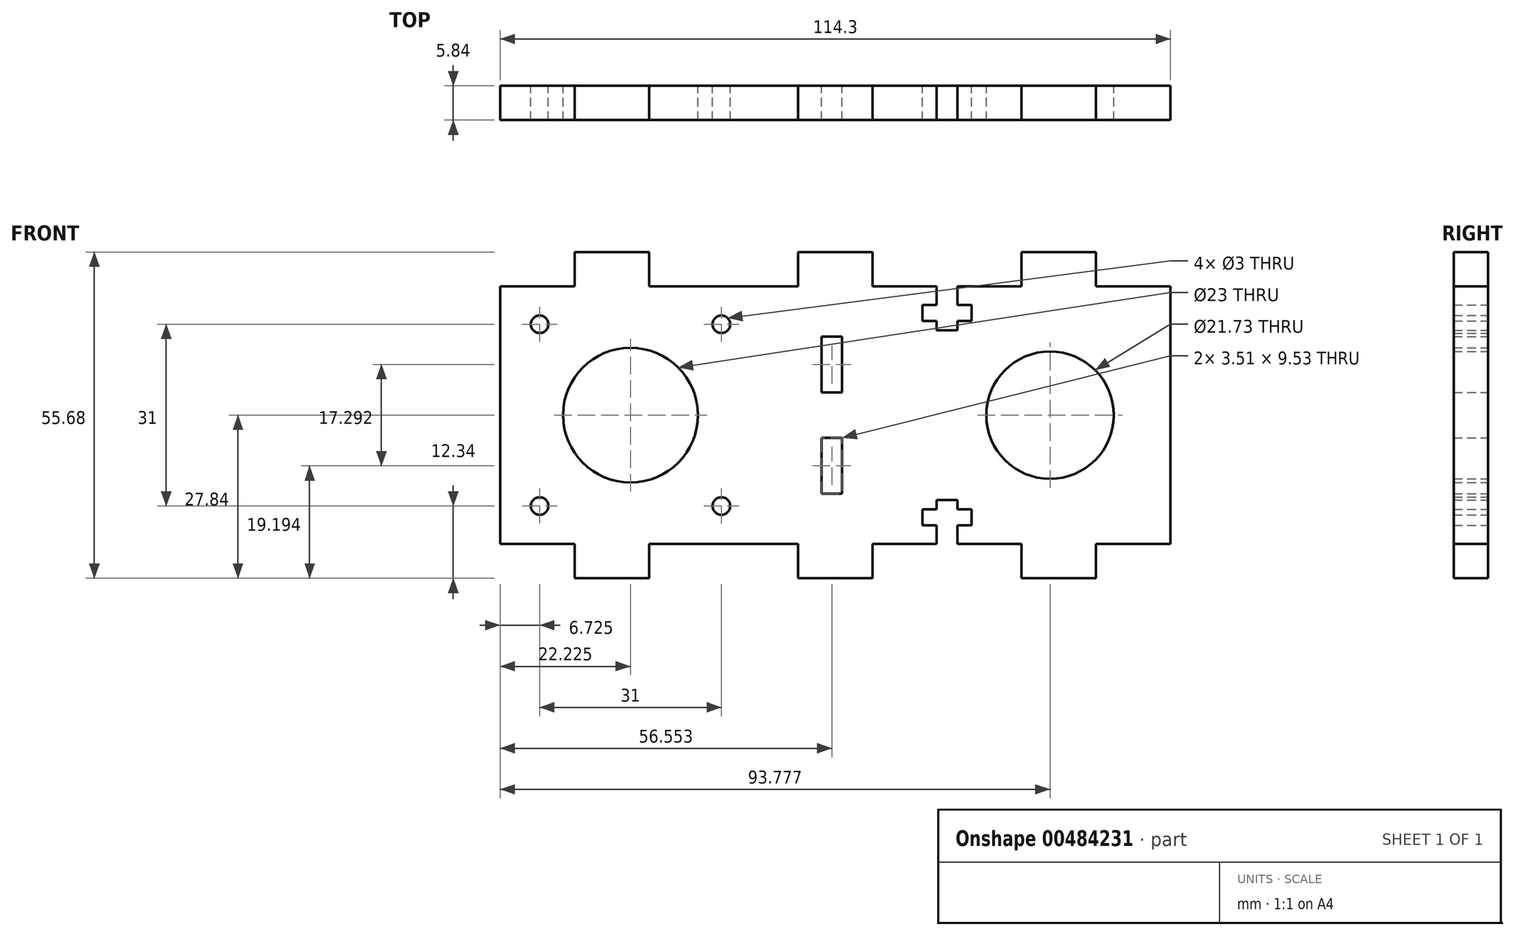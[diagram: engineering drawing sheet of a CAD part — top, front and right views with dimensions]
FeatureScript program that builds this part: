
annotation { "Feature Type Name" : "Feature", "Feature Type Description" : "" }
export const myFeature = defineFeature(function(context is Context, id is Id, definition is map)
    precondition{}
    {
        {
            var Q0;
            Q0=qCreatedBy(makeId("Front.planeOp"),FACE);
            var sketch = newSketch(context, id + "F0", { "sketchPlane" : qUnion([Q0])});
            skLineSegment(sketch, "E0.bottom", {"start": v(-57.15, 22) * mm, "end": v(-44.45, 22) * mm});
            skLineSegment(sketch, "E0.left", {"start": v(-57.15, 22) * mm, "end": v(-57.15, -22) * mm});
            skLineSegment(sketch, "E0.right", {"start": v(57.15, 22) * mm, "end": v(57.15, -22) * mm});
            skPoint(sketch, "E0.middle", {"position": v(0, 0) * mm});
            skCircle(sketch, "E1", {"center": v(-34.93, 0) * mm, "radius": 11.5 * mm});
            skCircle(sketch, "E2", {"center": v(36.63, 0) * mm, "radius": 10.86 * mm});
            skCircle(sketch, "E3", {"center": v(-50.43, 15.5) * mm, "radius": 1.5 * mm});
            skLineSegment(sketch, "E4", {"start": v(-34.93, 0) * mm, "end": v(-34.93, 11.5) * mm, "construction": true});
            skLineSegment(sketch, "E5", {"start": v(-34.93, 0) * mm, "end": v(-46.43, 0) * mm, "construction": true});
            skCircle(sketch, "E6.MirrorC", {"center": v(-19.43, 15.5) * mm, "radius": 1.5 * mm});
            skCircle(sketch, "E7.MirrorC", {"center": v(-19.43, -15.5) * mm, "radius": 1.5 * mm});
            skCircle(sketch, "E8.MirrorC", {"center": v(-50.43, -15.5) * mm, "radius": 1.5 * mm});
            skCircle(sketch, "E9", {"center": v(-34.93, 0) * mm, "radius": 5 * mm, "construction": true});
            skCircle(sketch, "E10", {"center": v(36.63, 0) * mm, "radius": 12.5 * mm, "construction": true});
            skLineSegment(sketch, "E11", {"start": v(-35.45, 4.97) * mm, "end": v(35.32, 12.43) * mm, "construction": true});
            skLineSegment(sketch, "E12.MirrorCS", {"start": v(-35.45, -4.97) * mm, "end": v(35.32, -12.43) * mm, "construction": true});
            skLineSegment(sketch, "E13", {"start": v(-0.6, 0) * mm, "end": v(-0.6, 12.84) * mm, "construction": true});
            skLineSegment(sketch, "E14.bottom", {"start": v(1.16, 13.4) * mm, "end": v(-2.35, 13.4) * mm});
            skLineSegment(sketch, "E14.top", {"start": v(1.16, 3.88) * mm, "end": v(-2.35, 3.88) * mm});
            skLineSegment(sketch, "E14.left", {"start": v(1.16, 13.4) * mm, "end": v(1.16, 3.88) * mm});
            skLineSegment(sketch, "E14.right", {"start": v(-2.35, 13.4) * mm, "end": v(-2.35, 3.88) * mm});
            skPoint(sketch, "E14.middle", {"position": v(-0.6, 8.65) * mm});
            skLineSegment(sketch, "E15.MirrorCS", {"start": v(1.16, -13.4) * mm, "end": v(-2.35, -13.4) * mm});
            skPoint(sketch, "E16.MirrorP", {"position": v(-0.6, -8.65) * mm});
            skLineSegment(sketch, "E17.MirrorCS", {"start": v(1.16, -13.4) * mm, "end": v(1.16, -3.88) * mm});
            skLineSegment(sketch, "E18.MirrorCS", {"start": v(1.16, -3.88) * mm, "end": v(-2.35, -3.88) * mm});
            skLineSegment(sketch, "E19.MirrorCS", {"start": v(-2.35, -13.4) * mm, "end": v(-2.35, -3.88) * mm});
            skLineSegment(sketch, "E20.top", {"start": v(-44.45, 27.84) * mm, "end": v(-31.75, 27.84) * mm});
            skLineSegment(sketch, "E20.left", {"start": v(-44.45, 22) * mm, "end": v(-44.45, 27.84) * mm});
            skLineSegment(sketch, "E20.right", {"start": v(-31.75, 22) * mm, "end": v(-31.75, 27.84) * mm});
            skPoint(sketch, "E20.middle", {"position": v(-38.1, 24.92) * mm});
            skLineSegment(sketch, "E21.trimOffspring", {"start": v(-31.75, 22) * mm, "end": v(-20.8, 22) * mm});
            skLineSegment(sketch, "E22.MirrorCS", {"start": v(44.45, 27.84) * mm, "end": v(31.75, 27.84) * mm});
            skLineSegment(sketch, "E23.MirrorCS", {"start": v(31.75, 22) * mm, "end": v(31.75, 27.84) * mm});
            skLineSegment(sketch, "E24.MirrorCS", {"start": v(44.45, 22) * mm, "end": v(44.45, 27.84) * mm});
            skPoint(sketch, "E25.MirrorP", {"position": v(38.1, 24.92) * mm});
            skLineSegment(sketch, "E26.MirrorCS", {"start": v(44.45, -22) * mm, "end": v(44.45, -27.84) * mm});
            skLineSegment(sketch, "E27.MirrorCS", {"start": v(-44.45, -27.84) * mm, "end": v(-31.75, -27.84) * mm});
            skLineSegment(sketch, "E28.MirrorCS", {"start": v(31.75, -22) * mm, "end": v(31.75, -27.84) * mm});
            skPoint(sketch, "E29.MirrorP", {"position": v(38.1, -24.92) * mm});
            skLineSegment(sketch, "E30.MirrorCS", {"start": v(44.45, -27.84) * mm, "end": v(31.75, -27.84) * mm});
            skPoint(sketch, "E31.MirrorP", {"position": v(-38.1, -24.92) * mm});
            skLineSegment(sketch, "E32.MirrorCS", {"start": v(-31.75, -22) * mm, "end": v(-31.75, -27.84) * mm});
            skLineSegment(sketch, "E33.MirrorCS", {"start": v(-44.45, -22) * mm, "end": v(-44.45, -27.84) * mm});
            skLineSegment(sketch, "E34.trimOffspring", {"start": v(-31.75, -22) * mm, "end": v(-20.8, -22) * mm});
            skLineSegment(sketch, "E35.trimOffspring", {"start": v(44.45, -22) * mm, "end": v(57.15, -22) * mm});
            skLineSegment(sketch, "E36.trimOffspring", {"start": v(44.45, 22) * mm, "end": v(57.15, 22) * mm});
            skLineSegment(sketch, "E37", {"start": v(-57.15, -22) * mm, "end": v(-44.45, -22) * mm});
            skLineSegment(sketch, "E38.top", {"start": v(-6.35, 27.84) * mm, "end": v(6.35, 27.84) * mm});
            skLineSegment(sketch, "E38.left", {"start": v(-6.35, 22) * mm, "end": v(-6.35, 27.84) * mm});
            skLineSegment(sketch, "E38.right", {"start": v(6.35, 22) * mm, "end": v(6.35, 27.84) * mm});
            skPoint(sketch, "E38.middle", {"position": v(0, 24.92) * mm});
            skLineSegment(sketch, "E39.trimOffspring", {"start": v(6.35, 22) * mm, "end": v(17.3, 22) * mm});
            skLineSegment(sketch, "E40.MirrorCS", {"start": v(6.35, -22) * mm, "end": v(6.35, -27.84) * mm});
            skPoint(sketch, "E41.MirrorP", {"position": v(0, -24.92) * mm});
            skLineSegment(sketch, "E42.MirrorCS", {"start": v(-6.35, -22) * mm, "end": v(-6.35, -27.84) * mm});
            skLineSegment(sketch, "E43.MirrorCS", {"start": v(-6.35, -27.84) * mm, "end": v(6.35, -27.84) * mm});
            skLineSegment(sketch, "E44.trimOffspring", {"start": v(6.35, -22) * mm, "end": v(17.3, -22) * mm});
            skLineSegment(sketch, "E45", {"start": v(-19.05, 22) * mm, "end": v(-19.05, -22) * mm, "construction": true});
            skPoint(sketch, "E46.middle", {"position": v(-19.05, -20.41) * mm});
            skPoint(sketch, "E47.middle", {"position": v(-19.05, -17.44) * mm});
            skPoint(sketch, "E48.middle", {"position": v(-19.05, -15.25) * mm});
            skLineSegment(sketch, "E49", {"start": v(-20.82, -16.05) * mm, "end": v(-20.8, -16.05) * mm});
            skLineSegment(sketch, "E50.trimOffspring", {"start": v(-17.3, -22) * mm, "end": v(-6.35, -22) * mm});
            skPoint(sketch, "E51.MirrorP", {"position": v(19.05, -15.25) * mm});
            skLineSegment(sketch, "E52.MirrorCS", {"start": v(17.3, -16.05) * mm, "end": v(17.3, -14.46) * mm});
            skLineSegment(sketch, "E53.MirrorCS", {"start": v(23.22, -18.83) * mm, "end": v(20.8, -18.83) * mm});
            skLineSegment(sketch, "E54.MirrorCS", {"start": v(17.3, -16.05) * mm, "end": v(14.88, -16.05) * mm});
            skLineSegment(sketch, "E55.MirrorCS", {"start": v(14.88, -18.83) * mm, "end": v(14.88, -16.05) * mm});
            skPoint(sketch, "E56.MirrorP", {"position": v(19.05, -17.44) * mm});
            skPoint(sketch, "E57.MirrorP", {"position": v(19.05, -20.41) * mm});
            skLineSegment(sketch, "E58.MirrorCS", {"start": v(20.8, -16.05) * mm, "end": v(20.8, -14.46) * mm});
            skLineSegment(sketch, "E59.MirrorCS", {"start": v(23.22, -18.83) * mm, "end": v(23.22, -16.05) * mm});
            skLineSegment(sketch, "E60.MirrorCS", {"start": v(23.22, -16.05) * mm, "end": v(20.8, -16.05) * mm});
            skLineSegment(sketch, "E61.MirrorCS", {"start": v(20.8, -14.46) * mm, "end": v(17.3, -14.46) * mm});
            skLineSegment(sketch, "E62.MirrorCS", {"start": v(20.8, -22) * mm, "end": v(20.8, -18.83) * mm});
            skLineSegment(sketch, "E63.MirrorCS", {"start": v(17.3, -18.83) * mm, "end": v(14.88, -18.83) * mm});
            skLineSegment(sketch, "E64.MirrorCS", {"start": v(17.3, -22) * mm, "end": v(17.3, -18.83) * mm});
            skLineSegment(sketch, "E65.trimOffspring", {"start": v(20.8, -22) * mm, "end": v(31.75, -22) * mm});
            skLineSegment(sketch, "E66.MirrorCS", {"start": v(23.22, 16.05) * mm, "end": v(20.8, 16.05) * mm});
            skLineSegment(sketch, "E67.MirrorCS", {"start": v(17.3, 18.83) * mm, "end": v(14.88, 18.83) * mm});
            skLineSegment(sketch, "E68.MirrorCS", {"start": v(23.22, 18.83) * mm, "end": v(20.8, 18.83) * mm});
            skLineSegment(sketch, "E69.MirrorCS", {"start": v(17.3, 16.05) * mm, "end": v(17.3, 14.46) * mm});
            skLineSegment(sketch, "E70.MirrorCS", {"start": v(17.3, 16.05) * mm, "end": v(14.88, 16.05) * mm});
            skLineSegment(sketch, "E71.MirrorCS", {"start": v(20.8, 16.05) * mm, "end": v(20.8, 14.46) * mm});
            skLineSegment(sketch, "E72.MirrorCS", {"start": v(-20.82, 16.05) * mm, "end": v(-20.8, 16.05) * mm});
            skLineSegment(sketch, "E73.MirrorCS", {"start": v(20.8, 14.46) * mm, "end": v(17.3, 14.46) * mm});
            skPoint(sketch, "E74.MirrorP", {"position": v(19.05, 20.41) * mm});
            skLineSegment(sketch, "E75.MirrorCS", {"start": v(14.88, 18.83) * mm, "end": v(14.88, 16.05) * mm});
            skPoint(sketch, "E76.MirrorP", {"position": v(-19.05, 20.41) * mm});
            skLineSegment(sketch, "E77.MirrorCS", {"start": v(23.22, 18.83) * mm, "end": v(23.22, 16.05) * mm});
            skLineSegment(sketch, "E78.MirrorCS", {"start": v(-17.3, 22) * mm, "end": v(-6.35, 22) * mm});
            skLineSegment(sketch, "E79.MirrorCS", {"start": v(20.8, 22) * mm, "end": v(20.8, 18.83) * mm});
            skPoint(sketch, "E80.MirrorP", {"position": v(19.05, 15.25) * mm});
            skLineSegment(sketch, "E81.MirrorCS", {"start": v(17.3, 22) * mm, "end": v(17.3, 18.83) * mm});
            skPoint(sketch, "E82.MirrorP", {"position": v(-19.05, 15.25) * mm});
            skPoint(sketch, "E83.MirrorP", {"position": v(-19.05, 17.44) * mm});
            skPoint(sketch, "E84.MirrorP", {"position": v(19.05, 17.44) * mm});
            skLineSegment(sketch, "E85.trimOffspring", {"start": v(20.8, 22) * mm, "end": v(31.75, 22) * mm});
            skLineSegment(sketch, "E86", {"start": v(-20.8, -22) * mm, "end": v(-17.3, -22) * mm});
            skLineSegment(sketch, "E87", {"start": v(-20.8, 22) * mm, "end": v(-17.3, 22) * mm});
            skPoint(sketch, "E88.orphan", {"position": v(-20.8, 14.46) * mm});
            skPoint(sketch, "E89.MirrorCS.end.orphan", {"position": v(-23.22, 16.05) * mm});
            skPoint(sketch, "E90.MirrorCS.end.orphan", {"position": v(-20.8, 18.83) * mm});
            skPoint(sketch, "E90.MirrorCS.start.orphan", {"position": v(-23.22, 18.83) * mm});
            skPoint(sketch, "E91.MirrorCS.start.orphan", {"position": v(-17.3, 18.83) * mm});
            skPoint(sketch, "E92.MirrorCS.start.orphan", {"position": v(-14.88, 18.83) * mm});
            skPoint(sketch, "E93.MirrorCS.end.orphan", {"position": v(-14.88, 16.05) * mm});
            skPoint(sketch, "E94.MirrorCS.end.orphan", {"position": v(-17.3, 14.46) * mm});
            skPoint(sketch, "E94.MirrorCS.start.orphan", {"position": v(-17.3, 16.05) * mm});
            skPoint(sketch, "E95.orphan", {"position": v(-20.8, -14.46) * mm});
            skPoint(sketch, "E48.right.end.orphan", {"position": v(-17.3, -14.46) * mm});
            skPoint(sketch, "E96.trimOffspring.start.orphan", {"position": v(-17.3, -16.05) * mm});
            skPoint(sketch, "E47.right.end.orphan", {"position": v(-14.88, -16.05) * mm});
            skPoint(sketch, "E97.trimOffspring.end.orphan", {"position": v(-14.88, -18.83) * mm});
            skPoint(sketch, "E46.right.end.orphan", {"position": v(-17.3, -18.83) * mm});
            skPoint(sketch, "E98.end.orphan", {"position": v(-20.8, -18.83) * mm});
            skPoint(sketch, "E47.left.start.orphan", {"position": v(-23.22, -18.83) * mm});
            skPoint(sketch, "E99.orphan", {"position": v(-23.22, -16.05) * mm});
            skSolve(sketch);
        }
        {
            var Q0;
            Q0 = qSketchRegion(id + "F0", true);
            extrude(context, id + "F1", {"entities" : qUnion([Q0]), "depth" : 5.84 * mm});
        }
    });
